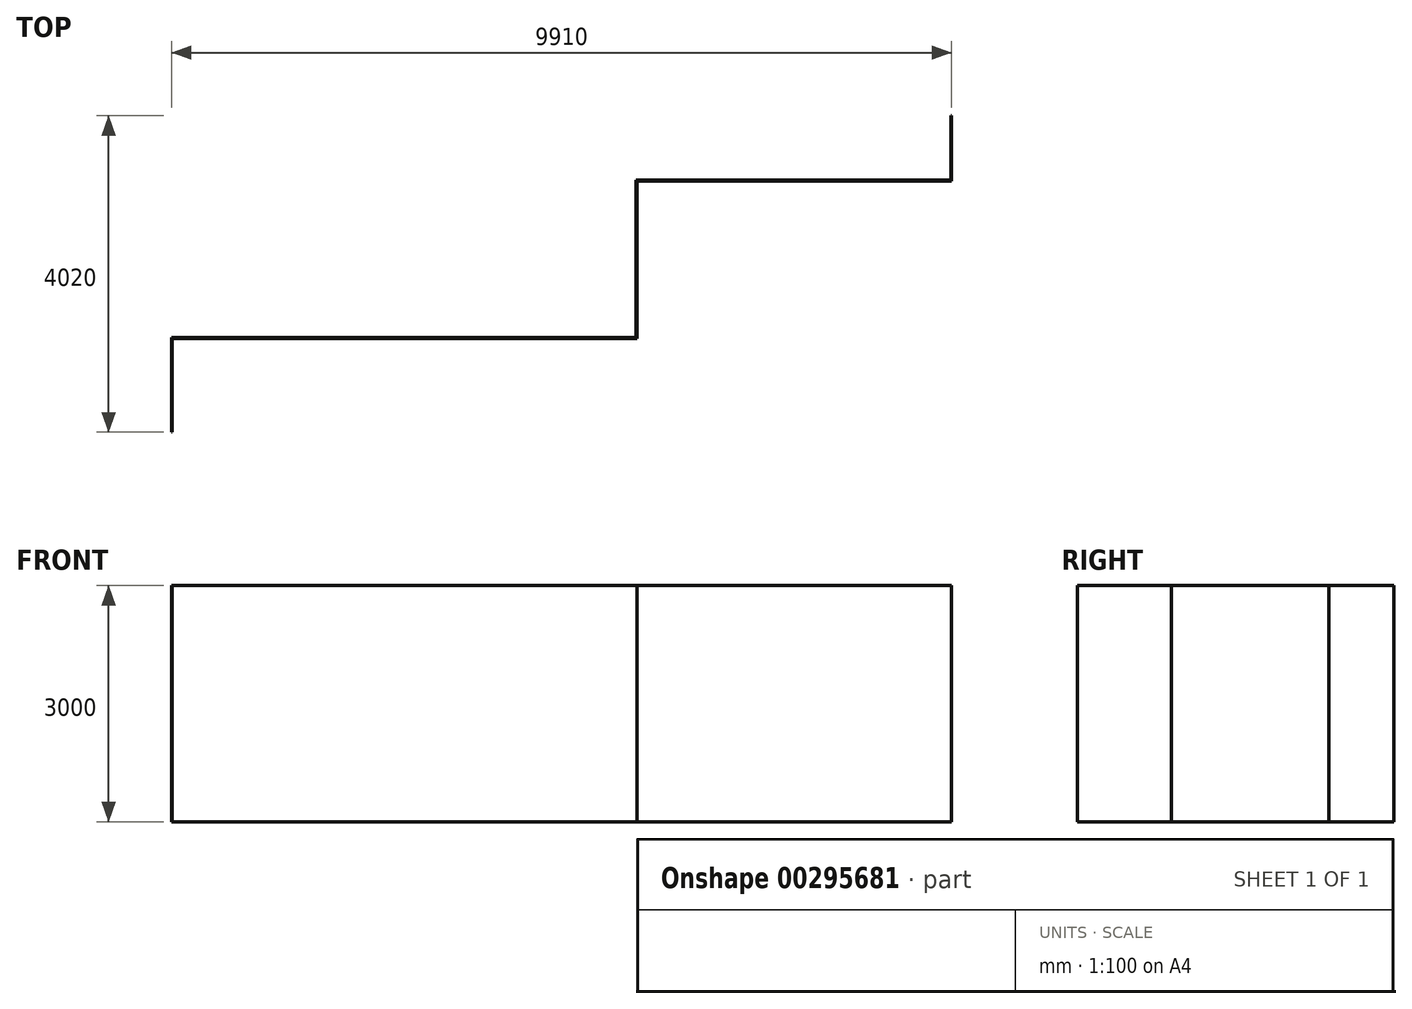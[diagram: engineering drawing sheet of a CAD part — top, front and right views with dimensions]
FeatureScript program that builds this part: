
annotation { "Feature Type Name" : "Feature", "Feature Type Description" : "" }
export const myFeature = defineFeature(function(context is Context, id is Id, definition is map)
    precondition{}
    {
        {
            var Q0;
            Q0=qCreatedBy(makeId("Top.planeOp"),FACE);
            var sketch = newSketch(context, id + "F0", { "sketchPlane" : qUnion([Q0])});
            skLineSegment(sketch, "E0", {"start": v(0, 0) * mm, "end": v(0, -820) * mm});
            skLineSegment(sketch, "E1", {"start": v(0, -820) * mm, "end": v(-4000, -820) * mm});
            skLineSegment(sketch, "E2", {"start": v(-4000, -820) * mm, "end": v(-4000, -2820) * mm});
            skLineSegment(sketch, "E3", {"start": v(-4000, -2820) * mm, "end": v(-9900, -2820) * mm});
            skLineSegment(sketch, "E4", {"start": v(-9900, -2820) * mm, "end": v(-9900, -4020) * mm});
            skLineSegment(sketch, "E5", {"start": v(-9900, -4020) * mm, "end": v(-9890, -4020) * mm});
            skLineSegment(sketch, "E6", {"start": v(-9890, -4020) * mm, "end": v(-9890, -2830) * mm});
            skLineSegment(sketch, "E7", {"start": v(-9890, -2830) * mm, "end": v(-3990, -2830) * mm});
            skLineSegment(sketch, "E8", {"start": v(-3990, -2830) * mm, "end": v(-3990, -830) * mm});
            skLineSegment(sketch, "E9", {"start": v(-3990, -830) * mm, "end": v(10, -830) * mm});
            skLineSegment(sketch, "E10", {"start": v(10, -830) * mm, "end": v(10, 0) * mm});
            skLineSegment(sketch, "E11", {"start": v(10, 0) * mm, "end": v(0, 0) * mm});
            skSolve(sketch);
        }
        {
            var Q0;
            Q0 = qSketchRegion(id + "F0", true);
            extrude(context, id + "F1", {"entities" : qUnion([Q0]), "depth" : 3000 * mm});
        }
    });
